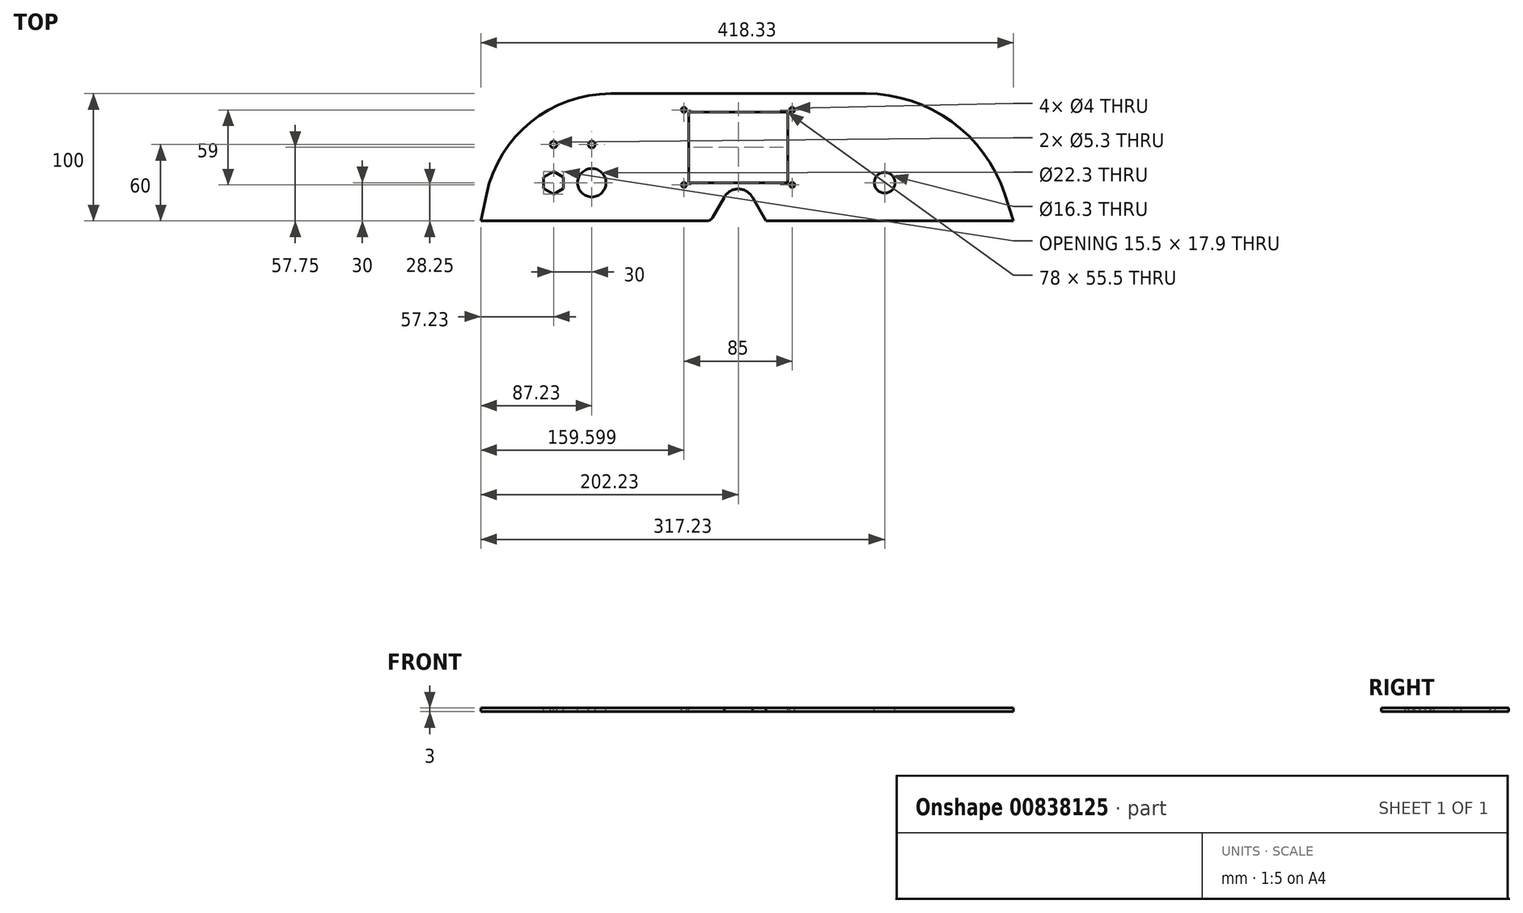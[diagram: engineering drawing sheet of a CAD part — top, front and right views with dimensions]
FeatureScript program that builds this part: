
annotation { "Feature Type Name" : "Feature", "Feature Type Description" : "" }
export const myFeature = defineFeature(function(context is Context, id is Id, definition is map)
    precondition{}
    {
        {
            var Q0;
            Q0=qCreatedBy(makeId("Top.planeOp"),FACE);
            var sketch = newSketch(context, id + "F0", { "sketchPlane" : qUnion([Q0])});
            skLineSegment(sketch, "E0", {"start": v(-202.23, 0) * mm, "end": v(-197.81, 20.8) * mm});
            skLineSegment(sketch, "E1", {"start": v(216.1, 0) * mm, "end": v(-202.23, 0) * mm});
            skLineSegment(sketch, "E2", {"start": v(-100, 100) * mm, "end": v(100, 100) * mm});
            skArc(sketch, "E3", {"start": v(-100, 100) * mm, "mid": v(-162.93, 77.71) * mm, "end": v(-197.81, 20.8) * mm});
            skArc(sketch, "E4", {"start": v(209.29, 20.8) * mm, "mid": v(167.49, 78.12) * mm, "end": v(100, 100) * mm});
            skLineSegment(sketch, "E5", {"start": v(0, 100) * mm, "end": v(0, 0) * mm, "construction": true});
            skLineSegment(sketch, "E6", {"start": v(216.1, 0) * mm, "end": v(209.29, 20.8) * mm});
            skSolve(sketch);
        }
        {
            var Q0;
            Q0 = qSketchRegion(id + "F0", true);
            extrude(context, id + "F1", {"entities" : qUnion([Q0]), "depth" : 3 * mm, "offsetDistance" : 25 * mm});
        }
        {
            var Q0;
            Q0=makeQuery(id+"F1.opExtrude","CAP_FACE",FACE,{"disambiguationData":[OSD([sQuery(id+"F0.wireOp",EDGE,"E0"),sQuery(id+"F0.wireOp",EDGE,"E1"),sQuery(id+"F0.wireOp",EDGE,"E2"),sQuery(id+"F0.wireOp",EDGE,"E3"),sQuery(id+"F0.wireOp",EDGE,"E4"),sQuery(id+"F0.wireOp",EDGE,"E6")])],"isStart":false});
            var sketch = newSketch(context, id + "F2", { "sketchPlane" : qUnion([Q0])});
            skCircle(sketch, "E7", {"center": v(0, 12.5) * mm, "radius": 12.6 * mm});
            skLineSegment(sketch, "E8", {"start": v(-11.1, 18.46) * mm, "end": v(-21.76, 0) * mm});
            skLineSegment(sketch, "E9", {"start": v(11.1, 18.46) * mm, "end": v(21.76, 0) * mm});
            skLineSegment(sketch, "E10", {"start": v(21.76, 0) * mm, "end": v(-21.76, 0) * mm});
            skSolve(sketch);
        }
        {
            var Q0;
            Q0 = qSketchRegion(id + "F2", true);
            extrude(context, id + "F3", {"entities" : qUnion([Q0]), "operationType" : NewBodyOperationType.REMOVE, "oppositeDirection" : true, "depth" : 25 * mm, "offsetDistance" : 25 * mm});
        }
        {
            var Q0;
            Q0=makeQuery(id+"F3.boolean.opBoolean","COPY",EDGE,{"derivedFrom":makeQuery(id+"F3.opExtrude","SWEPT_EDGE",EDGE,{"disambiguationData":[OSD([sQuery(id+"F0.wireOp",EDGE,"E1"),sQuery(id+"F2.wireOp",EDGE,"E8"),sQuery(id+"F2.wireOp",EDGE,"E10")])]})});
            var Q1;
            Q1=makeQuery(id+"F3.boolean.opBoolean","COPY",EDGE,{"derivedFrom":makeQuery(id+"F3.opExtrude","SWEPT_EDGE",EDGE,{"disambiguationData":[OSD([sQuery(id+"F0.wireOp",EDGE,"E1"),sQuery(id+"F2.wireOp",EDGE,"E9"),sQuery(id+"F2.wireOp",EDGE,"E10")])]})});
            fillet(context, id + "F4", {"entities" : qUnion([Q0, Q1]), "radius" : 5 * mm, "tangentPropagation" : true, "allowEdgeOverflow" : false});
        }
        {
            var Q0;
            Q0=makeQuery(id+"F1.opExtrude","CAP_FACE",FACE,{"disambiguationData":[OSD([sQuery(id+"F0.wireOp",EDGE,"E0"),sQuery(id+"F0.wireOp",EDGE,"E1"),sQuery(id+"F0.wireOp",EDGE,"E2"),sQuery(id+"F0.wireOp",EDGE,"E3"),sQuery(id+"F0.wireOp",EDGE,"E4"),sQuery(id+"F0.wireOp",EDGE,"E6")])],"isStart":false});
            var sketch = newSketch(context, id + "F5", { "sketchPlane" : qUnion([Q0])});
            skCircle(sketch, "E11.cCircle", {"center": v(-145, 30) * mm, "radius": 8.95 * mm, "construction": true});
            skLineSegment(sketch, "E11.0", {"start": v(-152.75, 34.47) * mm, "end": v(-145, 38.95) * mm});
            skLineSegment(sketch, "E11.1", {"start": v(-145, 38.95) * mm, "end": v(-137.25, 34.47) * mm});
            skLineSegment(sketch, "E11.2", {"start": v(-137.25, 34.47) * mm, "end": v(-137.25, 25.53) * mm});
            skLineSegment(sketch, "E11.3", {"start": v(-137.25, 25.53) * mm, "end": v(-145, 21.05) * mm});
            skLineSegment(sketch, "E11.4", {"start": v(-145, 21.05) * mm, "end": v(-152.75, 25.53) * mm});
            skLineSegment(sketch, "E11.5", {"start": v(-152.75, 25.53) * mm, "end": v(-152.75, 34.47) * mm});
            skCircle(sketch, "E12", {"center": v(-115, 30) * mm, "radius": 11.15 * mm});
            skCircle(sketch, "E13", {"center": v(-115, 60) * mm, "radius": 2.65 * mm});
            skCircle(sketch, "E14", {"center": v(-145, 60) * mm, "radius": 2.65 * mm});
            skSolve(sketch);
        }
        {
            var Q0;
            Q0 = qSketchRegion(id + "F5", true);
            extrude(context, id + "F6", {"entities" : qUnion([Q0]), "operationType" : NewBodyOperationType.REMOVE, "oppositeDirection" : true, "depth" : 25 * mm, "offsetDistance" : 25 * mm});
        }
        {
            var Q0;
            Q0=makeQuery(id+"F1.opExtrude","CAP_FACE",FACE,{"disambiguationData":[OSD([sQuery(id+"F0.wireOp",EDGE,"E0"),sQuery(id+"F0.wireOp",EDGE,"E1"),sQuery(id+"F0.wireOp",EDGE,"E2"),sQuery(id+"F0.wireOp",EDGE,"E3"),sQuery(id+"F0.wireOp",EDGE,"E4"),sQuery(id+"F0.wireOp",EDGE,"E6")])],"isStart":false});
            var sketch = newSketch(context, id + "F7", { "sketchPlane" : qUnion([Q0])});
            skLineSegment(sketch, "E15.bottom", {"start": v(-39, 30) * mm, "end": v(39, 30) * mm});
            skLineSegment(sketch, "E15.top", {"start": v(-39, 85.5) * mm, "end": v(39, 85.5) * mm});
            skLineSegment(sketch, "E15.left", {"start": v(-39, 30) * mm, "end": v(-39, 85.5) * mm});
            skLineSegment(sketch, "E15.right", {"start": v(39, 30) * mm, "end": v(39, 85.5) * mm});
            skCircle(sketch, "E16", {"center": v(-42.63, 28.25) * mm, "radius": 2 * mm});
            skCircle(sketch, "E17", {"center": v(-42.63, 87.25) * mm, "radius": 2 * mm});
            skCircle(sketch, "E18", {"center": v(42.37, 87.25) * mm, "radius": 2 * mm});
            skCircle(sketch, "E19", {"center": v(42.37, 28.25) * mm, "radius": 2 * mm});
            skLineSegment(sketch, "E20", {"start": v(0, 85.5) * mm, "end": v(0, 30) * mm, "construction": true});
            skSolve(sketch);
        }
        {
            var Q0;
            Q0 = qSketchRegion(id + "F7", true);
            extrude(context, id + "F8", {"entities" : qUnion([Q0]), "operationType" : NewBodyOperationType.REMOVE, "oppositeDirection" : true, "depth" : 25 * mm, "offsetDistance" : 25 * mm});
        }
        {
            var Q0;
            Q0=makeQuery(id+"F1.opExtrude","CAP_FACE",FACE,{"disambiguationData":[OSD([sQuery(id+"F0.wireOp",EDGE,"E0"),sQuery(id+"F0.wireOp",EDGE,"E1"),sQuery(id+"F0.wireOp",EDGE,"E2"),sQuery(id+"F0.wireOp",EDGE,"E3"),sQuery(id+"F0.wireOp",EDGE,"E4"),sQuery(id+"F0.wireOp",EDGE,"E6")])],"isStart":false});
            var sketch = newSketch(context, id + "F9", { "sketchPlane" : qUnion([Q0])});
            skCircle(sketch, "E21", {"center": v(115, 30) * mm, "radius": 8.15 * mm});
            skSolve(sketch);
        }
        {
            var Q0;
            Q0 = qSketchRegion(id + "F9", true);
            extrude(context, id + "F10", {"entities" : qUnion([Q0]), "operationType" : NewBodyOperationType.REMOVE, "oppositeDirection" : true, "depth" : 25 * mm, "offsetDistance" : 25 * mm});
        }
    });
